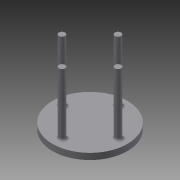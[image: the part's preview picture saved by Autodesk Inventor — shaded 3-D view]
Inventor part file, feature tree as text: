
AUTODESK INVENTOR PART (.ipt)
format: ipt  version: 2015 SP1 (Build 190203100, 203)  size: 104,448 bytes
history: native  units: mm
features: extrude x2, sketch x2, other x1, fillet x1
ambient origin geometry x8: Origin, YZ Plane, XZ Plane, XY Plane, X Axis, Y Axis, Z Axis, Center Point
bodies: Body1 (feature_tree)
feature tree (6):
  other  "Sólido1"
  extrude  "Extrusión1"  Depth=5.0mm TaperAngle=0.0deg
  extrude  "Extrusión2"  Depth=50.0mm
  fillet  "Empalme1"  Radius=50.0mm
  sketch  "Boceto1"  dims[d0=60.0mm d1=5.0mm d2=0.0mm]
  sketch  "Boceto2"  dims[d3=40.0mm d4=50.0mm d5=50.0mm d6=0.0mm d7=2.0mm]
